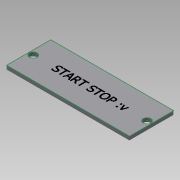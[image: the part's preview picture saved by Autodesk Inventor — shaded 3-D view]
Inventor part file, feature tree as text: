
AUTODESK INVENTOR PART (.ipt)
format: ipt  version: 2015 SP1 (Build 190203100, 203)  size: 84,480 bytes
history: native  units: mm
features: sketch x2, extrude x1, projected_geometry x1
ambient origin geometry x8: Origin, YZ Plane, XZ Plane, XY Plane, X Axis, Y Axis, Z Axis, Center Point
bodies: Solid1 (feature_tree)
feature tree (4):
  extrude  "Extrusion1"  Depth=19.939mm
  sketch  "Sketch2"  dims[d2=3.5mm d3=3.5mm d4=2.032mm d5=2.032mm d6=1.7mm d7=0.0mm]
  sketch  "Sketch1"  dims[d0=55.499mm d1=19.939mm]
  projected_geometry  "Projected Loop1"
